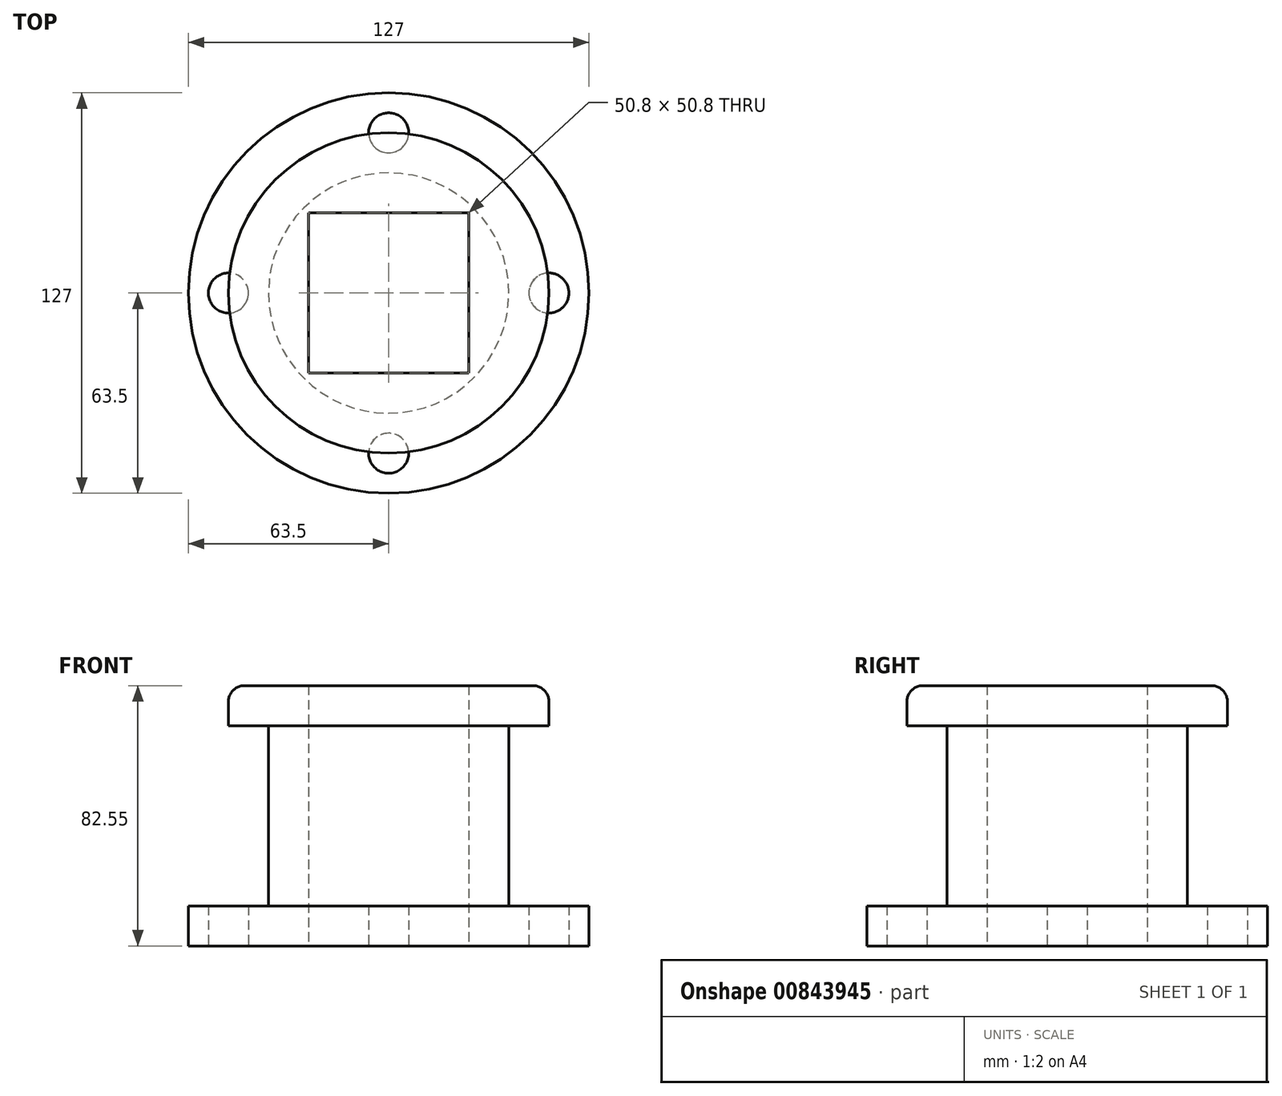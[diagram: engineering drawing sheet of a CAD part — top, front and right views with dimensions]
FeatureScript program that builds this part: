
annotation { "Feature Type Name" : "Feature", "Feature Type Description" : "" }
export const myFeature = defineFeature(function(context is Context, id is Id, definition is map)
    precondition{}
    {
        {
            var Q0;
            Q0=qCreatedBy(makeId("Top.planeOp"),FACE);
            var sketch = newSketch(context, id + "F0", { "sketchPlane" : qUnion([Q0])});
            skCircle(sketch, "E0", {"center": v(0, 0) * mm, "radius": 63.5 * mm});
            skCircle(sketch, "E1", {"center": v(0, 50.8) * mm, "radius": 6.35 * mm});
            skCircle(sketch, "E2", {"center": v(-50.8, 0) * mm, "radius": 6.35 * mm});
            skCircle(sketch, "E3", {"center": v(0, -50.8) * mm, "radius": 6.35 * mm});
            skCircle(sketch, "E4", {"center": v(50.8, 0) * mm, "radius": 6.35 * mm});
            skSolve(sketch);
        }
        {
            var Q0;
            Q0 = qSketchRegion(id + "F0", true);
            extrude(context, id + "F1", {"entities" : qUnion([Q0]), "depth" : 12.7 * mm, "offsetDistance" : 25.4 * mm});
        }
        {
            var Q0;
            Q0=makeQuery(id+"F1.opExtrude","CAP_FACE",FACE,{"disambiguationData":[OSD([sQuery(id+"F0.wireOp",EDGE,"E0"),sQuery(id+"F0.wireOp",EDGE,"E1"),sQuery(id+"F0.wireOp",EDGE,"E2"),sQuery(id+"F0.wireOp",EDGE,"E3"),sQuery(id+"F0.wireOp",EDGE,"E4")])],"isStart":false});
            var sketch = newSketch(context, id + "F2", { "sketchPlane" : qUnion([Q0])});
            skCircle(sketch, "E5", {"center": v(0, 0) * mm, "radius": 38.1 * mm});
            skSolve(sketch);
        }
        {
            var Q0;
            Q0 = qSketchRegion(id + "F2", true);
            var Q1;
            Q1 = qSketchRegion(id + "F4", true);
            extrude(context, id + "F3", {"entities" : qUnion([Q0, Q1]), "operationType" : NewBodyOperationType.ADD, "depth" : 57.15 * mm, "offsetDistance" : 25.4 * mm});
        }
        {
            var Q0;
            Q0=makeQuery(id+"F1.opExtrude","CAP_FACE",FACE,{"disambiguationData":[OSD([sQuery(id+"F0.wireOp",EDGE,"E0"),sQuery(id+"F0.wireOp",EDGE,"E1"),sQuery(id+"F0.wireOp",EDGE,"E2"),sQuery(id+"F0.wireOp",EDGE,"E3"),sQuery(id+"F0.wireOp",EDGE,"E4")])],"isStart":true});
            var sketch = newSketch(context, id + "F4", { "sketchPlane" : qUnion([Q0])});
            skCircle(sketch, "E6", {"center": v(0, 0) * mm, "radius": 50.8 * mm});
            skSolve(sketch);
        }
        {
            var Q0;
            Q0=makeQuery(id+"F3.opExtrude","CAP_FACE",FACE,{"disambiguationData":[OSD([sQuery(id+"F2.wireOp",EDGE,"E5")])],"isStart":false});
            var sketch = newSketch(context, id + "F5", { "sketchPlane" : qUnion([Q0])});
            skCircle(sketch, "E7", {"center": v(0, 0) * mm, "radius": 50.8 * mm});
            skSolve(sketch);
        }
        {
            var Q0;
            Q0 = qSketchRegion(id + "F5", true);
            extrude(context, id + "F6", {"entities" : qUnion([Q0]), "operationType" : NewBodyOperationType.ADD, "depth" : 12.7 * mm, "offsetDistance" : 25.4 * mm});
        }
        {
            var Q0;
            Q0=makeQuery(id+"F6.opExtrude","CAP_EDGE",EDGE,{"disambiguationData":[OSD([sQuery(id+"F5.wireOp",EDGE,"E7")])],"isStart":false});
            fillet(context, id + "F7", {"entities" : qUnion([Q0]), "radius" : 5.08 * mm, "tangentPropagation" : true, "allowEdgeOverflow" : false});
        }
        {
            var Q0;
            {var subQ0=sQuery(id+"F4.wireOp",EDGE,"E6");var subQ9=makeQuery(id+"F1.opExtrude","CAP_EDGE",EDGE,{"disambiguationData":[OSD([sQuery(id+"F0.wireOp",EDGE,"E3")])],"isStart":true});var subQ12=makeQuery(id+"F4.imprint","INTERSECT",VERTEX,{"disambiguationData":[OD(0.0)],"derivedFrom":[subQ9,subQ0]});Q0=makeQuery(id+"F4.imprint","IMPRINT",FACE,{"disambiguationData":[TD([[makeQuery(id+"F4.imprint","IMPRINT",EDGE,{"disambiguationData":[TD([[subQ12,1.0]])],"derivedFrom":subQ0}),1.0]])]});}
            var sketch = newSketch(context, id + "F8", { "sketchPlane" : qUnion([Q0])});
            skLineSegment(sketch, "E8.bottom", {"start": v(-25.4, 25.4) * mm, "end": v(25.4, 25.4) * mm});
            skLineSegment(sketch, "E8.top", {"start": v(-25.4, -25.4) * mm, "end": v(25.4, -25.4) * mm});
            skLineSegment(sketch, "E8.left", {"start": v(-25.4, 25.4) * mm, "end": v(-25.4, -25.4) * mm});
            skLineSegment(sketch, "E8.right", {"start": v(25.4, 25.4) * mm, "end": v(25.4, -25.4) * mm});
            skPoint(sketch, "E8.middle", {"position": v(0, 0) * mm});
            skSolve(sketch);
        }
        {
            var Q0;
            Q0 = qSketchRegion(id + "F8", true);
            extrude(context, id + "F9", {"entities" : qUnion([Q0]), "operationType" : NewBodyOperationType.REMOVE, "oppositeDirection" : true, "depth" : 82.55 * mm, "offsetDistance" : 25.4 * mm});
        }
    });
